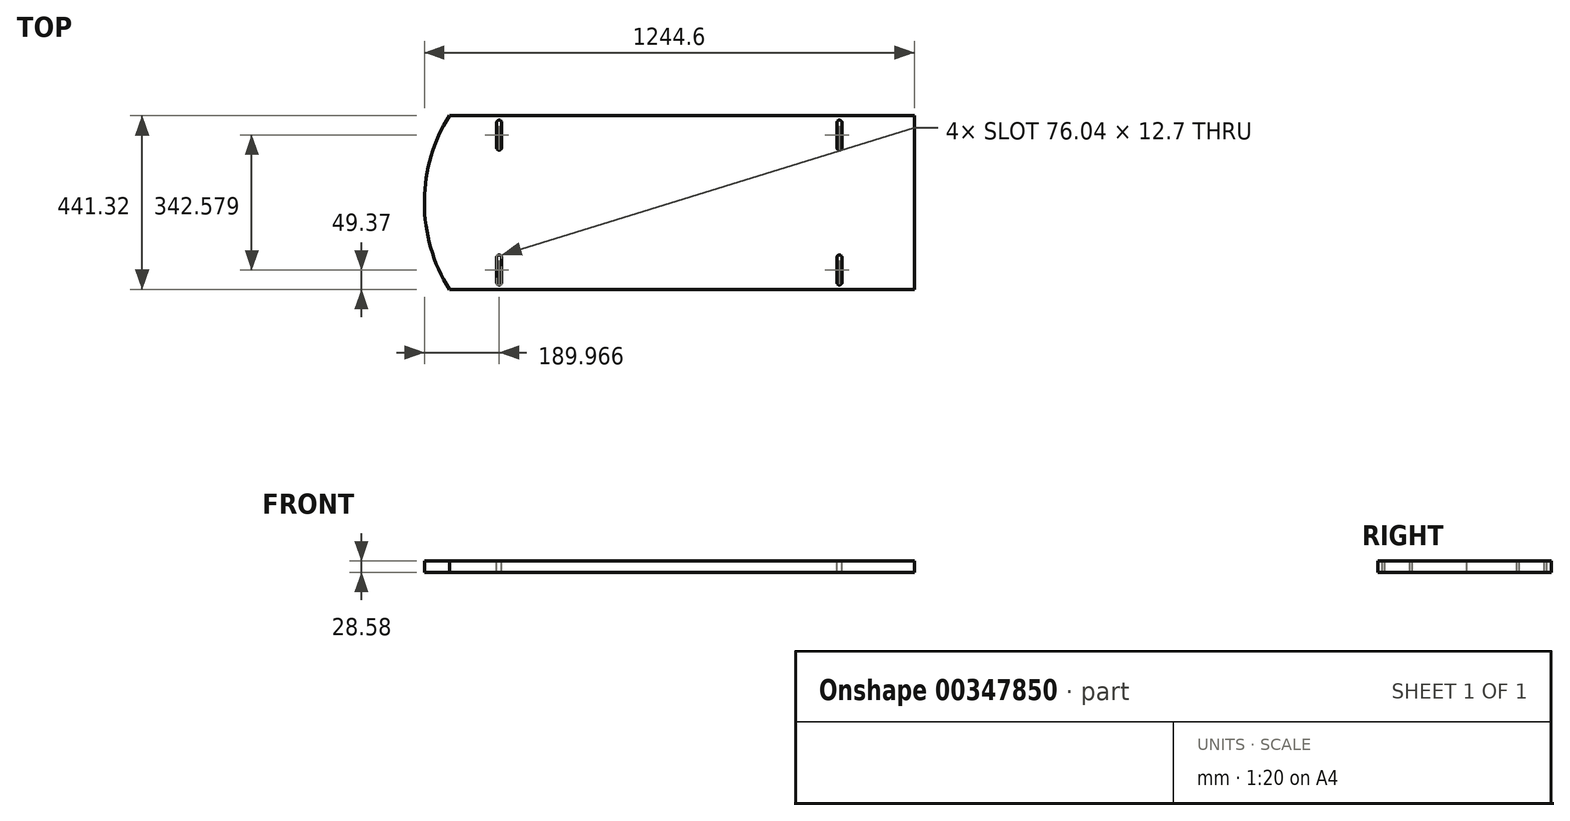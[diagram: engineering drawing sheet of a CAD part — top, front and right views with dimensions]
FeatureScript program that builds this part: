
annotation { "Feature Type Name" : "Feature", "Feature Type Description" : "" }
export const myFeature = defineFeature(function(context is Context, id is Id, definition is map)
    precondition{}
    {
        {
            var Q0;
            Q0=qCreatedBy(makeId("Front.planeOp"),FACE);
            var sketch = newSketch(context, id + "F0", { "sketchPlane" : qUnion([Q0])});
            skLineSegment(sketch, "E0.bottom", {"start": v(622.3, -14.29) * mm, "end": v(-622.3, -14.29) * mm});
            skLineSegment(sketch, "E0.top", {"start": v(622.3, 14.29) * mm, "end": v(-622.3, 14.29) * mm});
            skLineSegment(sketch, "E0.left", {"start": v(622.3, -14.29) * mm, "end": v(622.3, 14.29) * mm});
            skLineSegment(sketch, "E0.right", {"start": v(-622.3, -14.29) * mm, "end": v(-622.3, 14.29) * mm});
            skPoint(sketch, "E0.middle", {"position": v(0, 0) * mm});
            skSolve(sketch);
        }
        {
            var Q0;
            Q0=makeQuery(id+"F0.imprint","IMPRINT",FACE,{"disambiguationData":[TD([[makeQuery(id+"F0.imprint","IMPRINT",EDGE,{"derivedFrom":sQuery(id+"F0.wireOp",EDGE,"E0.bottom")}),-1.0]])]});
            extrude(context, id + "F1", {"entities" : qUnion([Q0]), "endBound" : BoundingType.SYMMETRIC, "oppositeDirection" : true, "depth" : 441.32 * mm});
        }
        {
            var Q0;
            Q0=makeQuery(id+"F1.opExtrude","SWEPT_FACE",FACE,{"disambiguationData":[OSD([sQuery(id+"F0.wireOp",EDGE,"E0.top")])]});
            var sketch = newSketch(context, id + "F2", { "sketchPlane" : qUnion([Q0])});
            skLineSegment(sketch, "E1", {"start": v(-773.46, 0) * mm, "end": v(899.63, 0) * mm, "construction": true});
            skPoint(sketch, "E1.startSnap0", {"position": v(-622.3, 0) * mm});
            skLineSegment(sketch, "E2", {"start": v(0, 220.66) * mm, "end": v(0, -220.66) * mm, "construction": true});
            skLineSegment(sketch, "E3.0", {"start": v(-425.98, 201.53) * mm, "end": v(-425.98, -341.4) * mm, "construction": true});
            skLineSegment(sketch, "E4.0", {"start": v(622.3, 6.35) * mm, "end": v(-622.3, 6.35) * mm});
            skLineSegment(sketch, "E5.0", {"start": v(-773.46, 139.7) * mm, "end": v(-438.68, 139.7) * mm, "construction": true});
            skLineSegment(sketch, "E6.MirrorCS", {"start": v(-773.46, -139.7) * mm, "end": v(899.63, -139.7) * mm, "construction": true});
            skLineSegment(sketch, "E7.MirrorCS", {"start": v(425.98, 201.53) * mm, "end": v(425.98, -341.4) * mm, "construction": true});
            skLineSegment(sketch, "E8.trimOffspring", {"start": v(-425.98, 139.7) * mm, "end": v(899.63, 139.7) * mm, "construction": true});
            skLineSegment(sketch, "E9.left", {"start": v(-425.98, 139.7) * mm, "end": v(-425.99, 202.88) * mm});
            skLineSegment(sketch, "E9.right", {"start": v(-438.68, 139.54) * mm, "end": v(-438.68, 203.04) * mm});
            skArc(sketch, "E10", {"start": v(-425.99, 202.88) * mm, "mid": v(-432.25, 209.3) * mm, "end": v(-438.68, 203.04) * mm});
            skArc(sketch, "E11", {"start": v(-438.68, 139.54) * mm, "mid": v(-432.25, 133.27) * mm, "end": v(-425.98, 139.7) * mm});
            skLineSegment(sketch, "E12.MirrorCS", {"start": v(0, -220.66) * mm, "end": v(0, 220.66) * mm, "construction": true});
            skLineSegment(sketch, "E13.MirrorCS", {"start": v(-438.68, -139.54) * mm, "end": v(-438.68, -203.04) * mm});
            skArc(sketch, "E14.MirrorCS", {"start": v(-425.99, -202.88) * mm, "mid": v(-432.25, -209.3) * mm, "end": v(-438.68, -203.04) * mm});
            skArc(sketch, "E15.MirrorCS", {"start": v(-438.68, -139.54) * mm, "mid": v(-432.25, -133.27) * mm, "end": v(-425.98, -139.7) * mm});
            skLineSegment(sketch, "E16.MirrorCS", {"start": v(-425.98, -139.7) * mm, "end": v(-425.99, -202.88) * mm});
            skLineSegment(sketch, "E17", {"start": v(-558.8, 299.07) * mm, "end": v(-558.8, -330.18) * mm, "construction": true});
            skArc(sketch, "E18", {"start": v(-558.8, 220.66) * mm, "mid": v(-622.3, 0) * mm, "end": v(-558.8, -220.66) * mm});
            skArc(sketch, "E19.MirrorCS", {"start": v(438.68, 139.54) * mm, "mid": v(432.25, 133.27) * mm, "end": v(425.98, 139.7) * mm});
            skArc(sketch, "E20.MirrorCS", {"start": v(438.68, -139.54) * mm, "mid": v(432.25, -133.27) * mm, "end": v(425.98, -139.7) * mm});
            skArc(sketch, "E21.MirrorCS", {"start": v(425.99, -202.88) * mm, "mid": v(432.25, -209.3) * mm, "end": v(438.68, -203.04) * mm});
            skLineSegment(sketch, "E22.MirrorCS", {"start": v(425.98, 139.7) * mm, "end": v(425.99, 202.88) * mm});
            skLineSegment(sketch, "E23.MirrorCS", {"start": v(438.68, 139.54) * mm, "end": v(438.68, 203.04) * mm});
            skArc(sketch, "E24.MirrorCS", {"start": v(425.99, 202.88) * mm, "mid": v(432.25, 209.3) * mm, "end": v(438.68, 203.04) * mm});
            skLineSegment(sketch, "E25.MirrorCS", {"start": v(425.98, -139.7) * mm, "end": v(425.99, -202.88) * mm});
            skArc(sketch, "E26.MirrorCS", {"start": v(558.8, 220.66) * mm, "mid": v(622.3, 0) * mm, "end": v(558.8, -220.66) * mm});
            skLineSegment(sketch, "E27.MirrorCS", {"start": v(438.68, -139.54) * mm, "end": v(438.68, -203.04) * mm});
            skPoint(sketch, "E28.MirrorP", {"position": v(622.3, 0) * mm});
            skLineSegment(sketch, "E29.MirrorCS", {"start": v(558.8, 299.07) * mm, "end": v(558.8, -330.18) * mm, "construction": true});
            skSolve(sketch);
        }
        {
            var Q0;
            Q0 = qSketchRegion(id + "F2", true);
            extrude(context, id + "F3", {"entities" : qUnion([Q0]), "operationType" : NewBodyOperationType.REMOVE, "oppositeDirection" : true, "depth" : 50.8 * mm});
        }
        {
            var Q0;
            {var subQ1=sQuery(id+"F0.wireOp",EDGE,"E0.top");var subQ4=sQuery(id+"F2.wireOp",EDGE,"E18");var subQ6=makeQuery(id+"F1.opExtrude","CAP_EDGE",EDGE,{"disambiguationData":[OSD([subQ1])],"isStart":false});var subQ8=makeQuery(id+"F2.imprint","INTERSECT",VERTEX,{"derivedFrom":[subQ6,subQ4]});Q0=makeQuery(id+"F2.imprint","IMPRINT",FACE,{"disambiguationData":[TD([[makeQuery(id+"F2.imprint","IMPRINT",EDGE,{"disambiguationData":[TD([[subQ8,-1.0]])],"derivedFrom":subQ4}),-1.0]])]});}
            var Q1;
            {var subQ0=sQuery(id+"F2.wireOp",EDGE,"E18");var subQ1=sQuery(id+"F0.wireOp",EDGE,"E0.top");var subQ2=makeQuery(id+"F1.opExtrude","CAP_EDGE",EDGE,{"disambiguationData":[OSD([subQ1])],"isStart":true});var subQ3=makeQuery(id+"F2.imprint","INTERSECT",VERTEX,{"derivedFrom":[subQ2,subQ0]});Q1=makeQuery(id+"F2.imprint","IMPRINT",FACE,{"disambiguationData":[TD([[makeQuery(id+"F2.imprint","IMPRINT",EDGE,{"disambiguationData":[TD([[subQ3,1.0]])],"derivedFrom":subQ0}),-1.0]])]});}
            var Q2;
            {var subQ1=sQuery(id+"F0.wireOp",EDGE,"E0.top");var subQ4=sQuery(id+"F2.wireOp",EDGE,"E26.MirrorCS");var subQ6=makeQuery(id+"F1.opExtrude","CAP_EDGE",EDGE,{"disambiguationData":[OSD([subQ1])],"isStart":false});var subQ8=makeQuery(id+"F2.imprint","INTERSECT",VERTEX,{"derivedFrom":[subQ6,subQ4]});Q2=makeQuery(id+"F2.imprint","IMPRINT",FACE,{"disambiguationData":[TD([[makeQuery(id+"F2.imprint","IMPRINT",EDGE,{"disambiguationData":[TD([[subQ8,-1.0]])],"derivedFrom":subQ4}),1.0]])]});}
            var Q3;
            {var subQ0=sQuery(id+"F2.wireOp",EDGE,"E26.MirrorCS");var subQ1=sQuery(id+"F0.wireOp",EDGE,"E0.top");var subQ2=makeQuery(id+"F1.opExtrude","CAP_EDGE",EDGE,{"disambiguationData":[OSD([subQ1])],"isStart":true});var subQ3=makeQuery(id+"F2.imprint","INTERSECT",VERTEX,{"derivedFrom":[subQ2,subQ0]});Q3=makeQuery(id+"F2.imprint","IMPRINT",FACE,{"disambiguationData":[TD([[makeQuery(id+"F2.imprint","IMPRINT",EDGE,{"disambiguationData":[TD([[subQ3,1.0]])],"derivedFrom":subQ0}),1.0]])]});}
            extrude(context, id + "F4", {"entities" : qUnion([Q0, Q1, Q2, Q3]), "operationType" : NewBodyOperationType.REMOVE, "oppositeDirection" : true, "depth" : 50.8 * mm});
        }
    });
